# Revit family: Haworth_JiveTable_PebbleSymmetricalBases
name_source: partatom
category: Furniture Systems
revit_build: Autodesk Revit 2018 (Build: 20170223_1515(x64)
units: mm (PartAtom-declared; Revit-internal decimal feet)

## family parameters
Always vertical = Yes
Cut with Voids When Loaded = No
OmniClass Number = 23.40.70.14.64.21
OmniClass Title = Systems Furniture
Part Type = Normal
Room Calculation Point = No
Round Connector Dimension = Use Diameter
Shared = No
Work Plane-Based = No

## types (1)
- Haworth_JiveTable_PebbleSymmetricalBases
    24in x 24in = No
    30in x 30in = No
    36in x 36in = No
    4 6 8 Column = Yes
    4 Column = Yes
    4 Column Leg Distance = 18"
    42in x 42in = No
    48in x 48in = No
    54in x 54in = No
    60in x 60in = Yes
    Actual Depth = 60"
    Actual Height = 29"
    Actual Width = 60"
    Assembly Code = E2020200
    Bridge Distance = 12"
    Casters = No
    Custom Size = No
    Description = Haworth Jive Table Pebble Symmetrical Bases - 60d 60w 29h - 4 Column - With Glides
    Glides = Yes
    Height = 29"
    Leg Height = 27 13/16"
    Manufacturer = Haworth, Inc.
    Max. Height = 42"
    Min. Height = 16"
    Model = Haworth Jive
    Revision Number = 0
    Size = Verify Final Dim. w/ Haworth
    Standard Depths = 24, 30, 36, 42, 48, 54, 60 in
    Standard Height = 16, 20, 29, 36, 42 in.
    Standard Width = 24, 30, 36, 42, 48, 54, 60 in.
    Support Distance = 14"
    Table Thickness = 1 3/16"
    URL = http://www.haworth.com
    URL - Product = http://www.haworth.com
    Warranty = http://www.haworth.com
    X Base = No
    X Base 2 3 Column = No

## geometry (parser evidence)
native form markers: Sweep x31
no freeform markers — native parametric forms only
